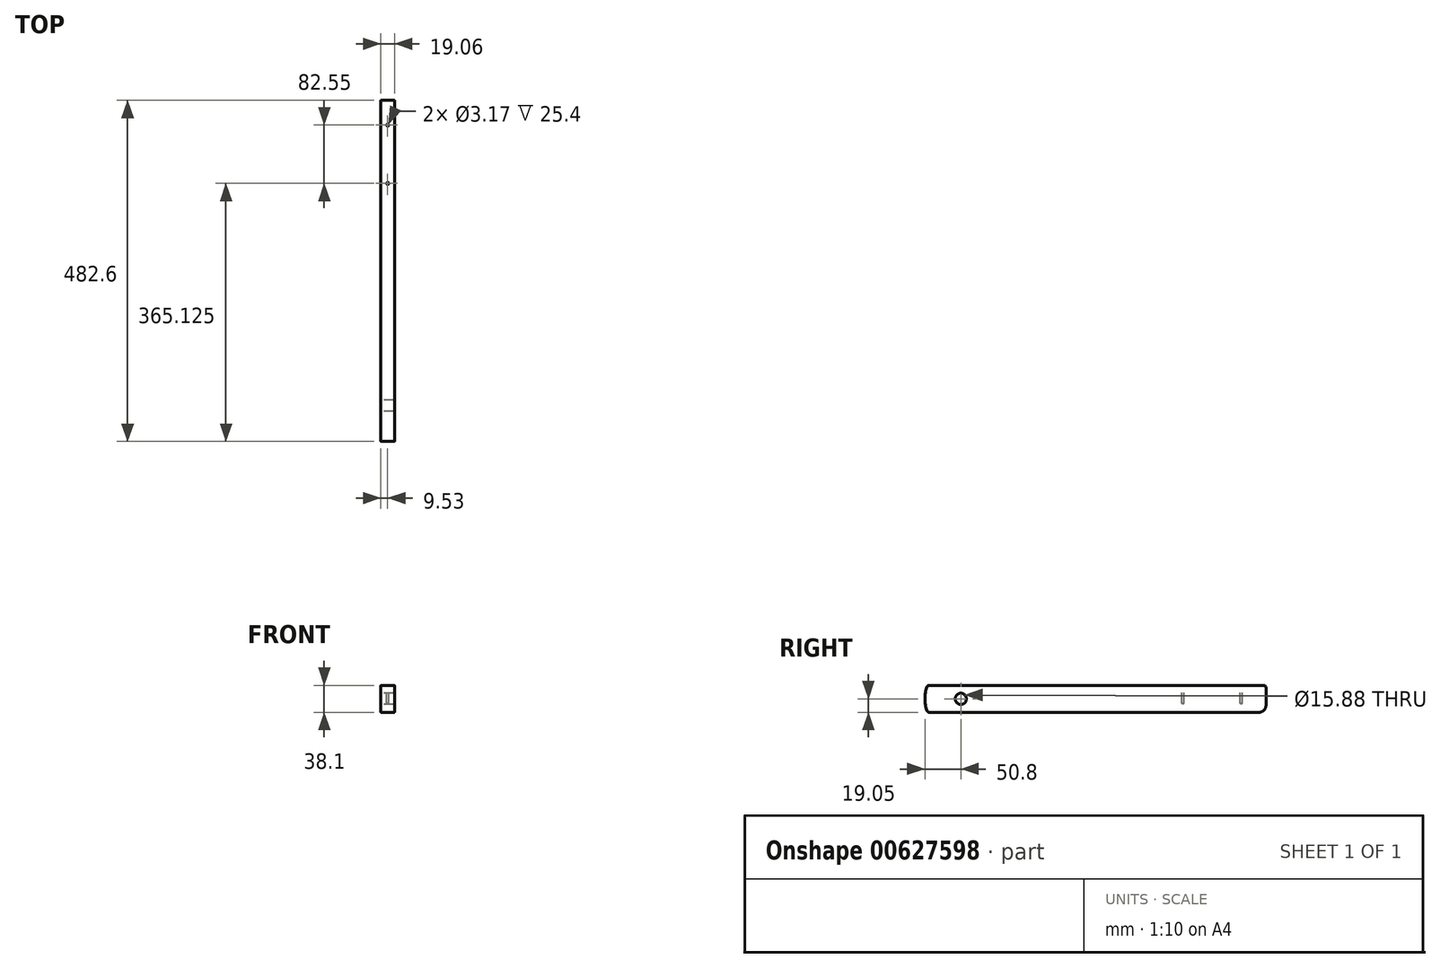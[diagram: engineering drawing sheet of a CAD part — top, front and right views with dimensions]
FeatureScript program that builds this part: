
annotation { "Feature Type Name" : "Feature", "Feature Type Description" : "" }
export const myFeature = defineFeature(function(context is Context, id is Id, definition is map)
    precondition{}
    {
        {
            var Q0;
            Q0=qCreatedBy(makeId("Right.planeOp"),FACE);
            var sketch = newSketch(context, id + "F0", { "sketchPlane" : qUnion([Q0])});
            skLineSegment(sketch, "E0.bottom", {"start": v(431.8, 19.05) * mm, "end": v(-47.1, 19.05) * mm});
            skLineSegment(sketch, "E0.top", {"start": v(431.8, -19.05) * mm, "end": v(-47.1, -19.05) * mm});
            skLineSegment(sketch, "E0.right", {"start": v(-50.8, 19.05) * mm, "end": v(-50.8, -19.05) * mm, "construction": true});
            skPoint(sketch, "E0.middle", {"position": v(0, 0) * mm});
            skCircle(sketch, "E1", {"center": v(0, 0) * mm, "radius": 7.94 * mm});
            skLineSegment(sketch, "E2", {"start": v(0, 0) * mm, "end": v(-50.8, 0) * mm, "construction": true});
            skArc(sketch, "E3", {"start": v(-47.1, 19.05) * mm, "mid": v(-50.8, 0) * mm, "end": v(-47.1, -19.05) * mm});
            skLineSegment(sketch, "E4", {"start": v(-50.8, 19.05) * mm, "end": v(-47.1, 19.05) * mm, "construction": true});
            skLineSegment(sketch, "E5", {"start": v(-47.1, -19.05) * mm, "end": v(-50.8, -19.05) * mm, "construction": true});
            skLineSegment(sketch, "E6", {"start": v(431.8, 19.05) * mm, "end": v(431.8, -19.05) * mm});
            skLineSegment(sketch, "E7", {"start": v(355.6, 19.05) * mm, "end": v(355.6, -19.05) * mm, "construction": true});
            skSolve(sketch);
        }
        {
            var Q0;
            Q0=qSketchRegion(id+"F0",true);
            extrude(context, id + "F1", {"entities" : qUnion([Q0]), "endBound" : BoundingType.SYMMETRIC, "depth" : 19.05 * mm, "offsetDistance" : 25.4 * mm});
        }
        {
            var Q0;
            Q0=makeQuery(id+"F1.opExtrude","SWEPT_FACE",FACE,{"disambiguationData":[OSD([sQuery(id+"F0.wireOp",EDGE,"E0.bottom")])]});
            var sketch = newSketch(context, id + "F2", { "sketchPlane" : qUnion([Q0])});
            skLineSegment(sketch, "E8", {"start": v(-9.53, 355.6) * mm, "end": v(9.53, 355.6) * mm, "construction": true});
            skLineSegment(sketch, "E9", {"start": v(0, 396.88) * mm, "end": v(0, 355.6) * mm, "construction": true});
            skCircle(sketch, "E10", {"center": v(0, 396.88) * mm, "radius": 1.59 * mm});
            skCircle(sketch, "E11", {"center": v(0, 314.33) * mm, "radius": 1.59 * mm});
            skLineSegment(sketch, "E12", {"start": v(0, 355.6) * mm, "end": v(0, 314.33) * mm, "construction": true});
            skSolve(sketch);
        }
        {
            var Q0;
            Q0=qSketchRegion(id+"F2",true);
            extrude(context, id + "F3", {"entities" : qUnion([Q0]), "operationType" : NewBodyOperationType.REMOVE, "oppositeDirection" : true, "depth" : 25.4 * mm, "offsetDistance" : 25.4 * mm});
        }
        {
            var Q0;
            Q0=makeQuery(id+"F1.opExtrude","SWEPT_EDGE",EDGE,{"disambiguationData":[OSD([sQuery(id+"F0.wireOp",EDGE,"E0.top"),sQuery(id+"F0.wireOp",EDGE,"E6")])]});
            fillet(context, id + "F4", {"entities" : qUnion([Q0]), "radius" : 9.52 * mm, "tangentPropagation" : true, "allowEdgeOverflow" : false});
        }
        {
            var Q0;
            Q0=makeQuery(id+"F1.opExtrude","SWEPT_EDGE",EDGE,{"disambiguationData":[OSD([sQuery(id+"F0.wireOp",EDGE,"E0.bottom"),sQuery(id+"F0.wireOp",EDGE,"E6")])]});
            var Q1;
            Q1=makeQuery(id+"F1.opExtrude","SWEPT_EDGE",EDGE,{"disambiguationData":[OSD([sQuery(id+"F0.wireOp",EDGE,"E0.top"),sQuery(id+"F0.wireOp",EDGE,"E3")])]});
            var Q2;
            Q2=makeQuery(id+"F1.opExtrude","SWEPT_EDGE",EDGE,{"disambiguationData":[OSD([sQuery(id+"F0.wireOp",EDGE,"E0.bottom"),sQuery(id+"F0.wireOp",EDGE,"E3")])]});
            fillet(context, id + "F5", {"entities" : qUnion([Q0, Q1, Q2]), "radius" : 3.17 * mm, "tangentPropagation" : true, "allowEdgeOverflow" : false});
        }
    });
